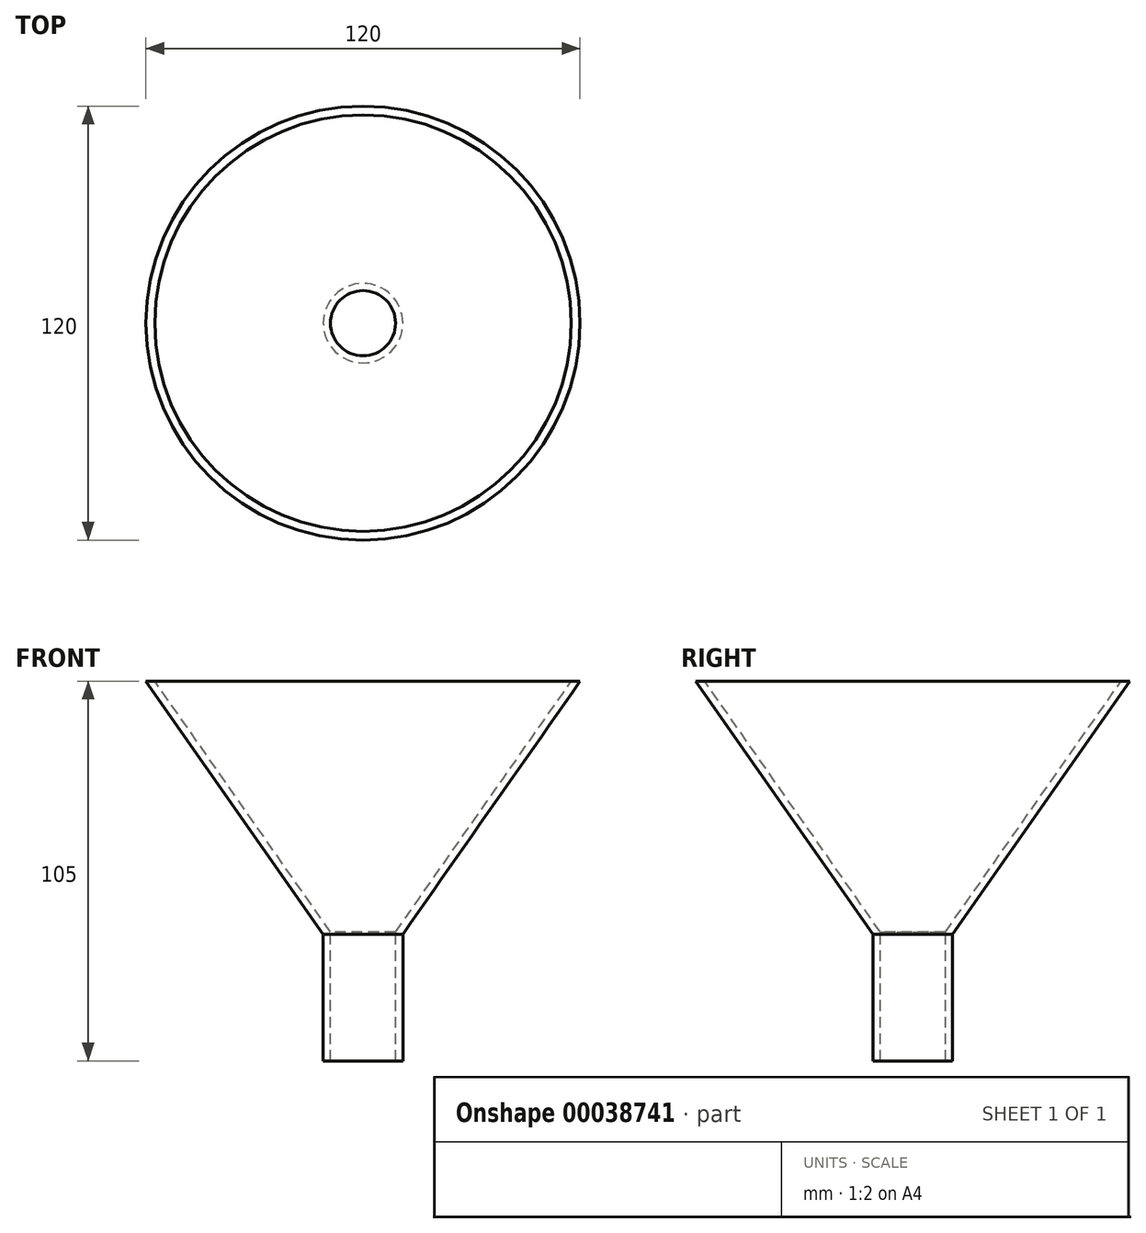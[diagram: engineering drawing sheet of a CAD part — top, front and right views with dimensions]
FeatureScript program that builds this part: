
annotation { "Feature Type Name" : "Feature", "Feature Type Description" : "" }
export const myFeature = defineFeature(function(context is Context, id is Id, definition is map)
    precondition{}
    {
        {
            var Q0;
            Q0=qCreatedBy(makeId("Top.planeOp"),FACE);
            var sketch = newSketch(context, id + "F0", { "sketchPlane" : qUnion([Q0])});
            skCircle(sketch, "E0", {"center": v(0, 0) * mm, "radius": 60 * mm});
            skSolve(sketch);
        }
        {
            var Q0;
            Q0=qCreatedBy(makeId("Top.planeOp"),FACE);
            cPlane(context, id + "F1", {"entities" : qUnion([Q0]), "cplaneType" : CPlaneType.OFFSET, "offset" : 70 * mm, "oppositeDirection" : true, "width" : 150 * mm, "height" : 150 * mm});
        }
        {
            var Q0;
            Q0=qCreatedBy(id+"F1.planeOp",FACE);
            var sketch = newSketch(context, id + "F2", { "sketchPlane" : qUnion([Q0])});
            skCircle(sketch, "E1", {"center": v(0, 0) * mm, "radius": 11 * mm});
            skSolve(sketch);
        }
        {
            var Q0;
            Q0=makeQuery(id+"F0.imprint","IMPRINT",FACE,{"disambiguationData":[TD([[makeQuery(id+"F0.imprint","IMPRINT",EDGE,{"derivedFrom":sQuery(id+"F0.wireOp",EDGE,"E0")}),1.0]])]});
            var Q1;
            Q1=makeQuery(id+"F2.imprint","IMPRINT",FACE,{"disambiguationData":[TD([[makeQuery(id+"F2.imprint","IMPRINT",EDGE,{"derivedFrom":sQuery(id+"F2.wireOp",EDGE,"E1")}),1.0]])]});
            loft(context, id + "F3", {"sheetProfilesArray" : [{ "sheetProfileEntities" : qUnion([Q0]) }, { "sheetProfileEntities" : qUnion([Q1]) }]});
        }
        {
            var Q0;
            Q0=makeQuery(id+"F3.opLoft","CAP_FACE",FACE,{"disambiguationData":[OSD([makeQuery(id+"F2.imprint","IMPRINT",FACE,{"disambiguationData":[TD([[makeQuery(id+"F2.imprint","IMPRINT",EDGE,{"derivedFrom":sQuery(id+"F2.wireOp",EDGE,"E1")}),1.0]])]})])],"isStart":true});
            extrude(context, id + "F4", {"entities" : qUnion([Q0]), "operationType" : NewBodyOperationType.ADD, "depth" : 35 * mm});
        }
        {
            var Q0;
            Q0=makeQuery(id+"F3.opLoft","CAP_FACE",FACE,{"disambiguationData":[OSD([makeQuery(id+"F0.imprint","IMPRINT",FACE,{"disambiguationData":[TD([[makeQuery(id+"F0.imprint","IMPRINT",EDGE,{"derivedFrom":sQuery(id+"F0.wireOp",EDGE,"E0")}),1.0]])]})])],"isStart":true});
            var Q1;
            Q1=makeQuery(id+"F4.opExtrude","CAP_FACE",FACE,{"disambiguationData":[OSD([makeQuery(id+"F2.imprint","IMPRINT",FACE,{"disambiguationData":[TD([[makeQuery(id+"F2.imprint","IMPRINT",EDGE,{"derivedFrom":sQuery(id+"F2.wireOp",EDGE,"E1")}),1.0]])]})])],"isStart":false});
            shell(context, id + "F5", {"entities" : qUnion([Q0, Q1]), "thickness" : 2 * mm});
        }
    });
